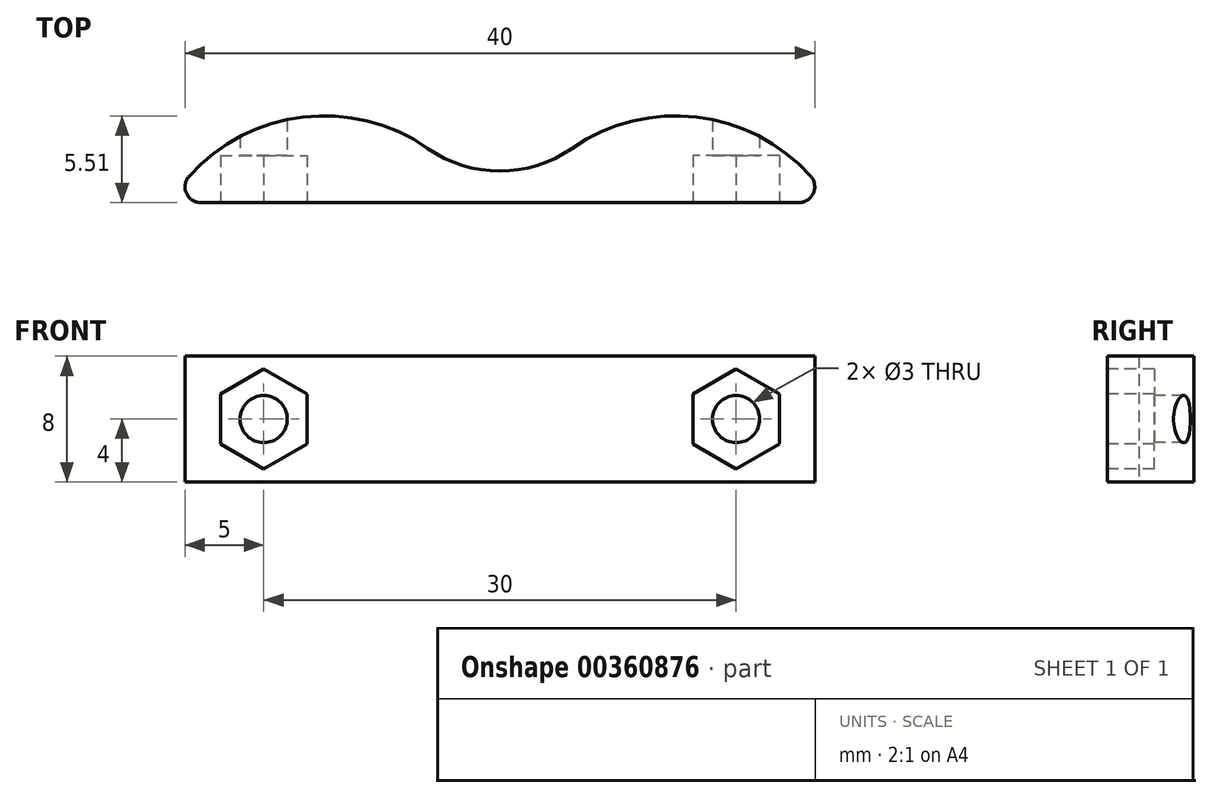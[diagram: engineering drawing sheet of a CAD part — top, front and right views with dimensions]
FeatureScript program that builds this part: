
annotation { "Feature Type Name" : "Feature", "Feature Type Description" : "" }
export const myFeature = defineFeature(function(context is Context, id is Id, definition is map)
    precondition{}
    {
        {
            var Q0;
            Q0=qCreatedBy(makeId("Top.planeOp"),FACE);
            var sketch = newSketch(context, id + "F0", { "sketchPlane" : qUnion([Q0])});
            skLineSegment(sketch, "E0.bottom", {"start": v(20, 5) * mm, "end": v(-20, 5) * mm});
            skLineSegment(sketch, "E0.top", {"start": v(20, -5) * mm, "end": v(-20, -5) * mm});
            skLineSegment(sketch, "E0.left", {"start": v(20, 5) * mm, "end": v(20, -5) * mm});
            skLineSegment(sketch, "E0.right", {"start": v(-20, 5) * mm, "end": v(-20, -5) * mm});
            skPoint(sketch, "E0.middle", {"position": v(0, 0) * mm});
            skPoint(sketch, "E1.endSnap0", {"position": v(0, 5) * mm});
            skCircle(sketch, "E2", {"center": v(0, 5) * mm, "radius": 8 * mm});
            skCircle(sketch, "E3", {"center": v(-19, -4) * mm, "radius": 1 * mm});
            skCircle(sketch, "E4", {"center": v(19, -4) * mm, "radius": 1 * mm});
            skCircle(sketch, "E5", {"center": v(-11.16, -10.99) * mm, "radius": 11.5 * mm});
            skCircle(sketch, "E6", {"center": v(11.16, -10.99) * mm, "radius": 11.5 * mm});
            skSolve(sketch);
        }
        {
            var Q0;
            {var subQ0=sQuery(id+"F0.wireOp",EDGE,"E5");var subQ1=sQuery(id+"F0.wireOp",EDGE,"E0.top");var subQ2=makeQuery(id+"F0.imprint","INTERSECT",VERTEX,{"derivedFrom":[subQ1,subQ0]});Q0=makeQuery(id+"F0.imprint","IMPRINT",FACE,{"disambiguationData":[TD([[makeQuery(id+"F0.imprint","IMPRINT",EDGE,{"disambiguationData":[TD([[subQ2,-1.0]])],"derivedFrom":subQ1}),-1.0]])]});}
            var Q1;
            {var subQ0=sQuery(id+"F0.wireOp",EDGE,"E3");var subQ1=makeQuery(id+"F0.imprint","INTERSECT",VERTEX,{"derivedFrom":[sQuery(id+"F0.wireOp",EDGE,"E0.right"),subQ0]});Q1=makeQuery(id+"F0.imprint","IMPRINT",FACE,{"disambiguationData":[TD([[makeQuery(id+"F0.imprint","IMPRINT",EDGE,{"disambiguationData":[TD([[subQ1,1.0]])],"derivedFrom":subQ0}),1.0]])]});}
            var Q2;
            {var subQ0=sQuery(id+"F0.wireOp",EDGE,"E6");var subQ1=sQuery(id+"F0.wireOp",EDGE,"E0.top");var subQ2=makeQuery(id+"F0.imprint","INTERSECT",VERTEX,{"derivedFrom":[subQ1,subQ0]});Q2=makeQuery(id+"F0.imprint","IMPRINT",FACE,{"disambiguationData":[TD([[makeQuery(id+"F0.imprint","IMPRINT",EDGE,{"disambiguationData":[TD([[subQ2,-1.0]])],"derivedFrom":subQ1}),-1.0]])]});}
            var Q3;
            {var subQ0=sQuery(id+"F0.wireOp",EDGE,"E6");var subQ1=sQuery(id+"F0.wireOp",EDGE,"E0.top");var subQ2=makeQuery(id+"F0.imprint","INTERSECT",VERTEX,{"derivedFrom":[subQ1,subQ0]});Q3=makeQuery(id+"F0.imprint","IMPRINT",FACE,{"disambiguationData":[TD([[makeQuery(id+"F0.imprint","IMPRINT",EDGE,{"disambiguationData":[TD([[subQ2,1.0]])],"derivedFrom":subQ1}),-1.0]])]});}
            var Q4;
            {var subQ0=sQuery(id+"F0.wireOp",EDGE,"E4");var subQ1=makeQuery(id+"F0.imprint","INTERSECT",VERTEX,{"derivedFrom":[sQuery(id+"F0.wireOp",EDGE,"E0.left"),subQ0]});Q4=makeQuery(id+"F0.imprint","IMPRINT",FACE,{"disambiguationData":[TD([[makeQuery(id+"F0.imprint","IMPRINT",EDGE,{"disambiguationData":[TD([[subQ1,-1.0]])],"derivedFrom":subQ0}),1.0]])]});}
            extrude(context, id + "F1", {"entities" : qUnion([Q0, Q1, Q2, Q3, Q4]), "depth" : 8 * mm});
        }
        {
            var Q0;
            Q0=makeQuery(id+"F1.opExtrude","SWEPT_FACE",FACE,{"disambiguationData":[OSD([sQuery(id+"F0.wireOp",EDGE,"E0.top")])]});
            var sketch = newSketch(context, id + "F2", { "sketchPlane" : qUnion([Q0])});
            skCircle(sketch, "E7", {"center": v(-15, 4) * mm, "radius": 1.5 * mm});
            skCircle(sketch, "E8", {"center": v(15, 4) * mm, "radius": 1.5 * mm});
            skSolve(sketch);
        }
        {
            var Q0;
            Q0 = qSketchRegion(id + "F2", true);
            extrude(context, id + "F3", {"entities" : qUnion([Q0]), "operationType" : NewBodyOperationType.REMOVE, "oppositeDirection" : true, "depth" : 25 * mm});
        }
        {
            var Q0;
            Q0=makeQuery(id+"F1.opExtrude","SWEPT_FACE",FACE,{"disambiguationData":[OSD([sQuery(id+"F0.wireOp",EDGE,"E0.top")])]});
            var sketch = newSketch(context, id + "F4", { "sketchPlane" : qUnion([Q0])});
            skCircle(sketch, "E9.cCircle", {"center": v(-15, 4) * mm, "radius": 2.75 * mm, "construction": true});
            skLineSegment(sketch, "E9.0", {"start": v(-12.25, 5.59) * mm, "end": v(-12.25, 2.41) * mm});
            skLineSegment(sketch, "E9.1", {"start": v(-12.25, 2.41) * mm, "end": v(-15, 0.82) * mm});
            skLineSegment(sketch, "E9.2", {"start": v(-15, 0.82) * mm, "end": v(-17.75, 2.41) * mm});
            skLineSegment(sketch, "E9.3", {"start": v(-17.75, 2.41) * mm, "end": v(-17.75, 5.59) * mm});
            skLineSegment(sketch, "E9.4", {"start": v(-17.75, 5.59) * mm, "end": v(-15, 7.18) * mm});
            skLineSegment(sketch, "E9.5", {"start": v(-15, 7.18) * mm, "end": v(-12.25, 5.59) * mm});
            skPoint(sketch, "E9.0.midPoint", {"position": v(-12.25, 4) * mm});
            skCircle(sketch, "E10.cCircle", {"center": v(15, 4) * mm, "radius": 2.75 * mm, "construction": true});
            skLineSegment(sketch, "E10.0", {"start": v(12.25, 2.41) * mm, "end": v(12.25, 5.59) * mm});
            skLineSegment(sketch, "E10.1", {"start": v(12.25, 5.59) * mm, "end": v(15, 7.18) * mm});
            skLineSegment(sketch, "E10.2", {"start": v(15, 7.18) * mm, "end": v(17.75, 5.59) * mm});
            skLineSegment(sketch, "E10.3", {"start": v(17.75, 5.59) * mm, "end": v(17.75, 2.41) * mm});
            skLineSegment(sketch, "E10.4", {"start": v(17.75, 2.41) * mm, "end": v(15, 0.82) * mm});
            skLineSegment(sketch, "E10.5", {"start": v(15, 0.82) * mm, "end": v(12.25, 2.41) * mm});
            skPoint(sketch, "E10.0.midPoint", {"position": v(12.25, 4) * mm});
            skSolve(sketch);
        }
        {
            var Q0;
            Q0 = qSketchRegion(id + "F4", true);
            extrude(context, id + "F5", {"entities" : qUnion([Q0]), "operationType" : NewBodyOperationType.REMOVE, "oppositeDirection" : true, "depth" : 3 * mm});
        }
    });
